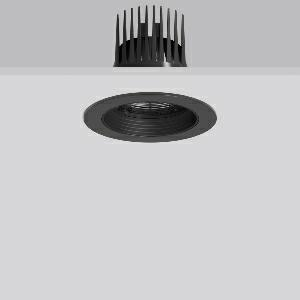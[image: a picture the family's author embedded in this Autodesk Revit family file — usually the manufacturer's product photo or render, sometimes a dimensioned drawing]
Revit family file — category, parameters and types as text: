
# Revit family: heledon_maxi_e_901769_003_1_76_5e39
name_source: partatom
category: Lighting Fixtures
units: mm (PartAtom-declared; Revit-internal decimal feet)

## family parameters
Cut with Voids When Loaded = No
Host = Face
Light Source = No
Part Type = Normal
Room Calculation Point = No
Round Connector Dimension = Use Diameter
Shared = No

## types (1)
- HELEDON maxi E (1 x LED Modul 940, 3800 lm, 4000)
    Apparent Load = 35 VA
    Approval mark = CE
    CIE Flux Codes = 96 100 100 100 100
    Color Rendering = 92
    Color Temperature = 4000
    Default Elevation = 1800 mm
    Description = Series: HELEDON maxi
Round recessed downlight. Housing: die-cast aluminium, powder-coated. Black plastic ring and recessed LED to prevent glare from the side. Optical assembly with lens made of plastic (polycarbonate) for the best homogeneous light distribution - can be changed without tools. Best colour rendering index Ra>90. Suitable for Recessed ceiling mounting. Installation without tools thanks to spring fastening system. Including separate LED converter with connecting cable 600 mm.High quality converter without flickering and stroboscopic effect. Through-wiring box (5 pole) available as accessory. The following accessories can be mounted without use of tools: interchangeable lenses, decorative glasses, honeycomb louvre, clear and frosted diffusers, white interchangeable plastic ring. 
Colour: deep black, matt (RAL 9005)
Diameter: 162 mm
Height: 3 mm
Cut-out diameter: 152 mm
Recess height: 200 mm
Luminaire: recess height: 135 mm
Lamp: LED
Socket: without socket
Colour temperature: 4000K
Colour rendering index (CRI): 92
System power: 35 W
Rated luminous flux: 3800 lm
Luminous efficiency: 109 lm/W
Control gear: Converter, dimmable, DALI
Protection class: II
Type of protection: IP 20
    Height = 0 mm  [stored 0 ft]
    Lamp = 1 x LED Modul 940
    Lamp Light Flux = 3800 lm
    Lamp count = 1
    Length = 162 mm
    Lifetime = 50000 h
    Luminous efficacy = 109 lm/W
    Manufacturer = RZB
    ModVariant = No
    Model = 901769.003.1.76
    Mounting Place = Ceiling
    Mounting Type = Recessed
    Number of Poles = 1
    OnlyDefault = Yes
    Power Factor = 1
    Product Name = HELEDON maxi E
    Product group = Recessed downlights
    ProductGroupID = 402
    Protection Class = Protection class II
    Protection Degree = IP 20
    RLX_Detail_Level = 1
    RLX_Emergency_Light_Flux = 0 lm
    RLX_Emergency_Type = 0
    RLX_Emergency_Type_DB = No
    RlxData = <blob elided: 120341 chars, md5=e2e3419a>
    Socket = socket
    Standby Power = 0 W
    System Light Flux = 3800 lm
    System Power = 35 W
    Type Comments = Product without accessories
    Type Image = 901663.003.jpg
    URL = http://relux.com
    VarID = ---
    Voltage = 230 V
    Voltage Range = 220-240 V
    Weight = 0.00 kg
    Width = 0 mm  [stored 0 ft]

note: [stored X ft] marks values corroborated as IEEE doubles in the binary element streams (Revit-internal decimal feet)

## geometry (parser evidence)
native form markers: Blend x4, Sweep x12
no freeform markers — native parametric forms only
